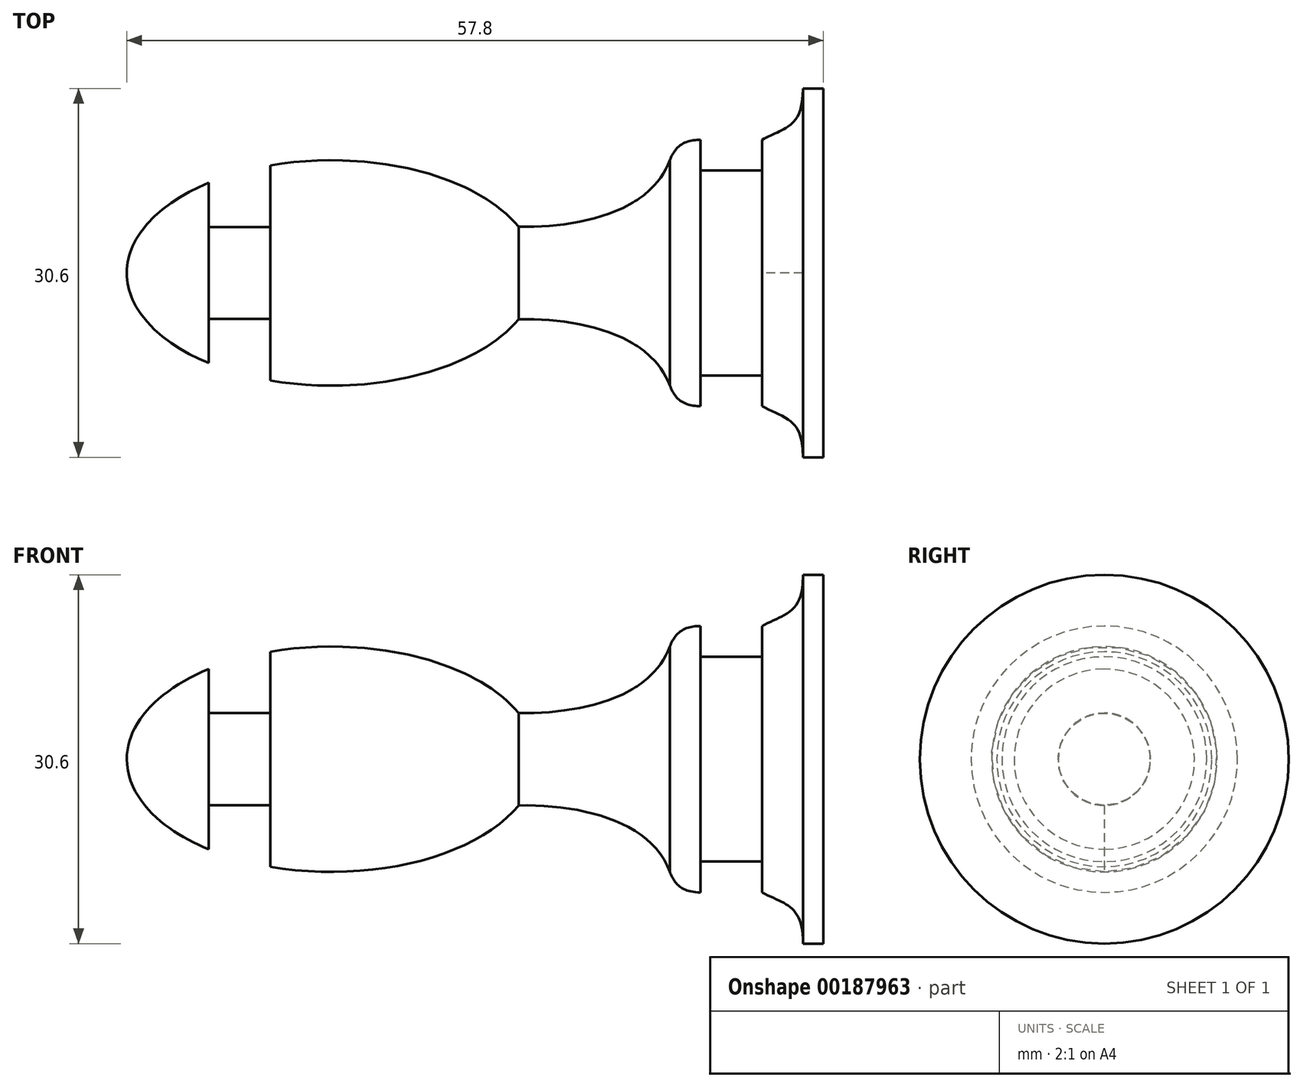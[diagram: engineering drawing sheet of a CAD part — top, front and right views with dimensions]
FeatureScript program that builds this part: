
annotation { "Feature Type Name" : "Feature", "Feature Type Description" : "" }
export const myFeature = defineFeature(function(context is Context, id is Id, definition is map)
    precondition{}
    {
        {
            var Q0;
            Q0=qCreatedBy(makeId("Front.planeOp"),FACE);
            var sketch = newSketch(context, id + "F0", { "sketchPlane" : qUnion([Q0])});
            skLineSegment(sketch, "E0", {"start": v(0, 0) * mm, "end": v(-34, 0) * mm});
            skLineSegment(sketch, "E1", {"start": v(0, 0) * mm, "end": v(0, 9) * mm});
            skPoint(sketch, "E2.orphan", {"position": v(-34, 9) * mm});
            skPoint(sketch, "E3.visualSharp", {"position": v(-34.34, -0.25) * mm});
            skLineSegment(sketch, "E4", {"start": v(-34, 0) * mm, "end": v(-34, 0) * mm});
            skLineSegment(sketch, "E5", {"start": v(-27, 2.25) * mm, "end": v(-30, 2.25) * mm});
            skLineSegment(sketch, "E6", {"start": v(-30, 2.25) * mm, "end": v(-30, 4.4) * mm});
            skLineSegment(sketch, "E7", {"start": v(-27, 2.25) * mm, "end": v(-27, 5.25) * mm});
            skEllipticalArc(sketch, "E8.trimOffspring", {});
            skPoint(sketch, "E9.start.orphan", {"position": v(-24.77, 2.25) * mm});
            skLineSegment(sketch, "E10", {"start": v(-24, 5.5) * mm, "end": v(-24, 0) * mm});
            skEllipticalArc(sketch, "E11.trimOffspring", {});
            skEllipticalArc(sketch, "E12", {});
            skPoint(sketch, "E13.MirrorCS.start.orphan", {"position": v(-21, 2.25) * mm});
            skPoint(sketch, "E14.MirrorCS.start.orphan", {"position": v(-18, 2.25) * mm});
            skPoint(sketch, "E15.orphan", {"position": v(-18, 4.4) * mm});
            skEllipticalArc(sketch, "E16.trimOffspring", {});
            skLineSegment(sketch, "E17", {"start": v(0, 9) * mm, "end": v(-1, 9) * mm});
            skLineSegment(sketch, "E18", {"start": v(-3, 6.5) * mm, "end": v(-3, 5) * mm});
            skLineSegment(sketch, "E19", {"start": v(-3, 5) * mm, "end": v(-6, 5) * mm});
            skLineSegment(sketch, "E20", {"start": v(-6, 5) * mm, "end": v(-6, 6.5) * mm});
            skFitSpline(sketch, "E21", {"points": [v(-1, 9) * mm, v(-3, 6.5) * mm], "startDerivative": vector(0, -5.74) * mm, "endDerivative": vector(-3.4, -1.84) * mm});
            skPoint(sketch, "E22", {"position": v(-1, 7.75) * mm});
            skPoint(sketch, "E23", {"position": v(-2, 6.5) * mm});
            skPoint(sketch, "E24", {"position": v(-6.75, 6.5) * mm});
            skFitSpline(sketch, "E25", {"points": [v(-6, 6.5) * mm, v(-7.5, 5.5) * mm], "startDerivative": vector(-3.03, 0) * mm, "endDerivative": vector(-0.61, -1.46) * mm});
            skLineSegment(sketch, "E26", {"start": v(-7.5, 5.5) * mm, "end": v(-7.5, 0) * mm});
            skLineSegment(sketch, "E27", {"start": v(-7.5, 0) * mm, "end": v(0, 0) * mm});
            skPoint(sketch, "E28.trimOffspring.end.orphan", {"position": v(-7.5, 6.5) * mm});
            skPoint(sketch, "E29.orphan", {"position": v(-1, 6.5) * mm});
            skLineSegment(sketch, "E30", {"start": v(0, 0) * mm, "end": v(0, 0) * mm});
            skFitSpline(sketch, "E31", {"points": [v(-14.88, 2.26) * mm, v(-7.5, 5.5) * mm], "startDerivative": vector(9.45, -0.18) * mm, "endDerivative": vector(2.66, 7.33) * mm});
            const initialGuessF0  = {"E8.trimOffspring": [-0.024, 0, -1, 0, 0.01, 0.0055, 5.355890089177974, 0], "E11.trimOffspring": [-0.024, 0, -1, 0, 0.01, 0.0055, 4.40769632636929, 5.017081634400087], "E12": [-0.024, 0, 0, 1, 0.0055, 0.01, 4.71238898038469, 0.3046926540153976], "E16.trimOffspring": [-0.024, 0, 0, 1, 0.0055, 0.01, 0.6435011087932843, 1.570796326794897]};
            skSetInitialGuess(sketch, initialGuessF0);
            skSolve(sketch);
        }
        {
            var Q0;
            Q0=qSketchRegion(id+"F0",true);
            var Q1;
            Q1=sQuery(id+"F0.wireOp",EDGE,"E0");
            revolve(context, id + "F1", {"entities" : qUnion([Q0]), "axis" : qUnion([Q1]), "revolveType" : RevolveType.FULL});
        }
        {
            var Q0;
            Q0=makeQuery(id+"F1.opRevolve","SWEPT_BODY",BODY,{"disambiguationData":[OSD([sQuery(id+"F0.wireOp",EDGE,"E0"),sQuery(id+"F0.wireOp",EDGE,"E5"),sQuery(id+"F0.wireOp",EDGE,"E6"),sQuery(id+"F0.wireOp",EDGE,"E7"),sQuery(id+"F0.wireOp",EDGE,"E12"),sQuery(id+"F0.wireOp",EDGE,"E16.trimOffspring"),sQuery(id+"F0.wireOp",EDGE,"E1"),sQuery(id+"F0.wireOp",EDGE,"E17"),sQuery(id+"F0.wireOp",EDGE,"E18"),sQuery(id+"F0.wireOp",EDGE,"E19"),sQuery(id+"F0.wireOp",EDGE,"E20"),sQuery(id+"F0.wireOp",EDGE,"E21"),sQuery(id+"F0.wireOp",EDGE,"E25"),sQuery(id+"F0.wireOp",EDGE,"E27"),sQuery(id+"F0.wireOp",EDGE,"E31")])]});
            var Q1;
            Q1=qCreatedBy(makeId("Origin.pointOp"),VERTEX);
            transform(context, id + "F2", {"entities" : qUnion([Q0]), "transformType" : TransformType.SCALE_UNIFORMLY, "scale" : 1.7, "scalePoint" : qUnion([Q1]), "makeCopy" : false});
        }
    });
